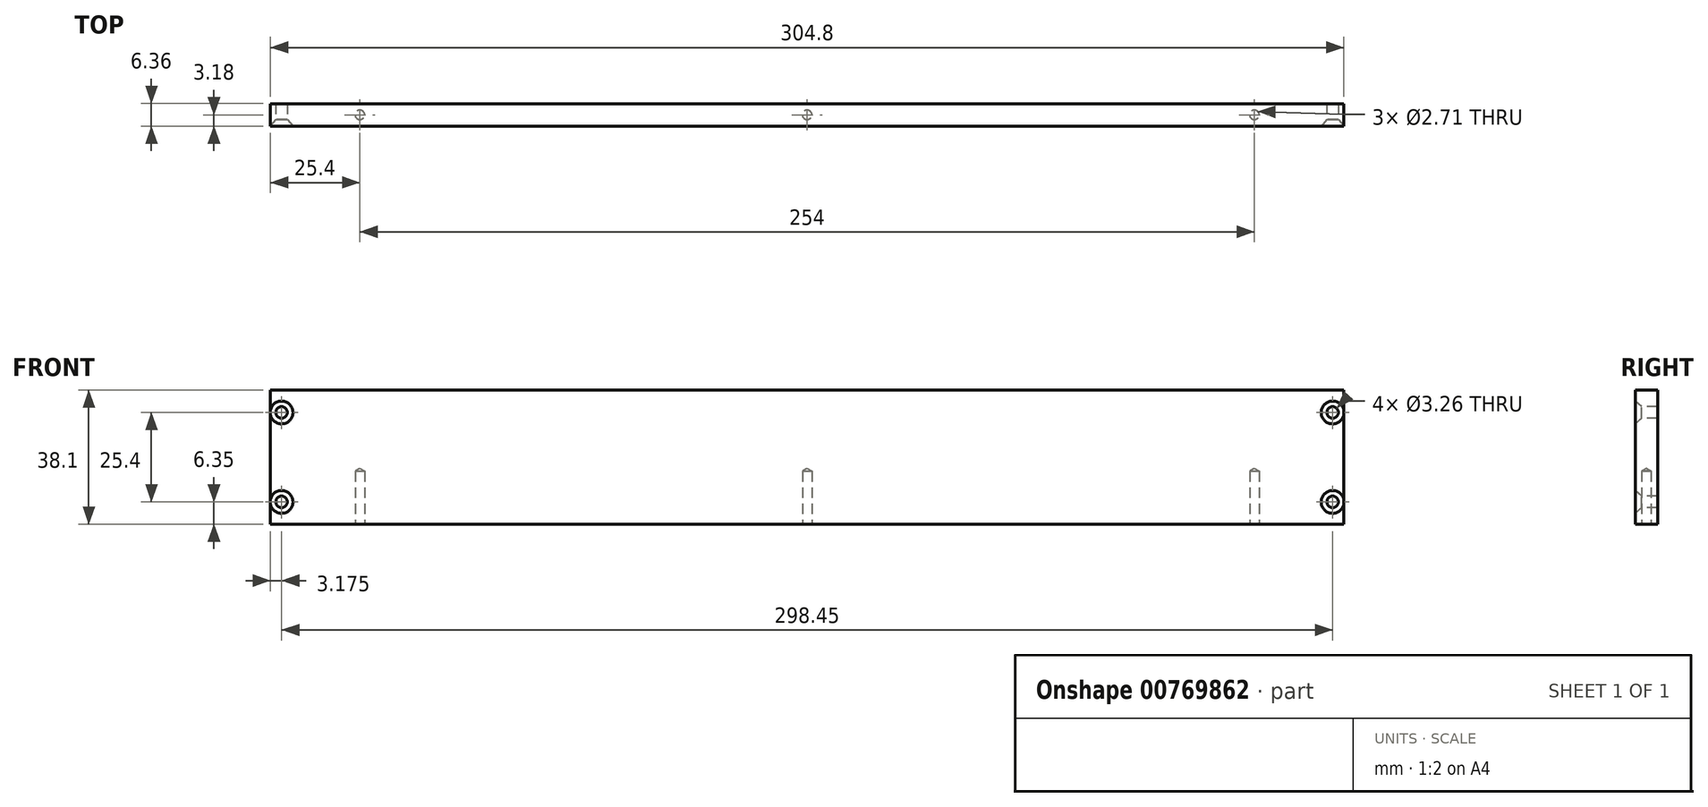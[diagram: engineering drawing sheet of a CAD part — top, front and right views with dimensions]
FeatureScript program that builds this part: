
annotation { "Feature Type Name" : "Feature", "Feature Type Description" : "" }
export const myFeature = defineFeature(function(context is Context, id is Id, definition is map)
    precondition{}
    {
        {
            var Q0;
            Q0=qCreatedBy(makeId("Top.planeOp"),FACE);
            var sketch = newSketch(context, id + "F0", { "sketchPlane" : qUnion([Q0])});
            skLineSegment(sketch, "E0.bottom", {"start": v(-152.4, 3.17) * mm, "end": v(152.4, 3.17) * mm});
            skLineSegment(sketch, "E0.top", {"start": v(-152.4, -3.18) * mm, "end": v(152.4, -3.18) * mm});
            skLineSegment(sketch, "E0.left", {"start": v(-152.4, 3.17) * mm, "end": v(-152.4, -3.18) * mm});
            skLineSegment(sketch, "E0.right", {"start": v(152.4, 3.17) * mm, "end": v(152.4, -3.18) * mm});
            skLineSegment(sketch, "E1", {"start": v(-152.4, 3.17) * mm, "end": v(152.4, -3.17) * mm, "construction": true});
            skSolve(sketch);
        }
        {
            var Q0;
            Q0=qSketchRegion(id+"F0",true);
            extrude(context, id + "F1", {"entities" : qUnion([Q0]), "depth" : 38.1 * mm, "offsetDistance" : 25.4 * mm});
        }
        {
            var Q0;
            Q0=makeQuery(id+"F1.opExtrude","CAP_FACE",FACE,{"disambiguationData":[OSD([sQuery(id+"F0.wireOp",EDGE,"E0.bottom"),sQuery(id+"F0.wireOp",EDGE,"E0.top"),sQuery(id+"F0.wireOp",EDGE,"E0.left"),sQuery(id+"F0.wireOp",EDGE,"E0.right")])],"isStart":true});
            var sketch = newSketch(context, id + "F2", { "sketchPlane" : qUnion([Q0])});
            skLineSegment(sketch, "E2", {"start": v(-152.4, 0) * mm, "end": v(152.4, 0) * mm, "construction": true});
            skPoint(sketch, "E3", {"position": v(-127, 0) * mm});
            skPoint(sketch, "E4", {"position": v(0, 0) * mm});
            skPoint(sketch, "E5", {"position": v(127, 0) * mm});
            skSolve(sketch);
        }
        {
            var Q0;
            Q0=sQuery(id+"F2.wireOp",VERTEX,"E3");
            var Q1;
            Q1=sQuery(id+"F2.wireOp",VERTEX,"E5");
            var Q2;
            Q2=sQuery(id+"F2.wireOp",VERTEX,"E4");
            var Q3;
            Q3=makeQuery(id+"F1.opExtrude","SWEPT_BODY",BODY,{"disambiguationData":[OSD([sQuery(id+"F0.wireOp",EDGE,"E0.bottom"),sQuery(id+"F0.wireOp",EDGE,"E0.top"),sQuery(id+"F0.wireOp",EDGE,"E0.left"),sQuery(id+"F0.wireOp",EDGE,"E0.right")])]});
            hole(context, id + "F3", {"style" : HoleStyle.SIMPLE, "endStyle" : HoleEndStyle.BLIND, "standardTappedOrClearance" : lookupTablePath({ "standard" : "ANSI", "engagement" : "75%", "pitch" : "32 tpi", "size" : "#6", "type" : "Tapped" }), "standardBlindInLast" : lookupTablePath({ "standard" : "ANSI", "engagement" : "75%", "pitch" : "32 tpi", "size" : "#6", "type" : "Tapped" }), "holeDiameter" : 2.7 * mm, "majorDiameter" : 3.5 * mm, "showTappedDepth" : true, "holeDepth" : 15.08 * mm, "tappedDepth" : 12.7 * mm, "tapClearance" : 3, "locations" : qUnion([Q0, Q1, Q2]), "scope" : qUnion([Q3])});
        }
        {
            var Q0;
            Q0=makeQuery(id+"F1.opExtrude","SWEPT_FACE",FACE,{"disambiguationData":[OSD([sQuery(id+"F0.wireOp",EDGE,"E0.top")])]});
            var sketch = newSketch(context, id + "F4", { "sketchPlane" : qUnion([Q0])});
            skLineSegment(sketch, "E6", {"start": v(-149.22, 38.1) * mm, "end": v(-149.22, 0) * mm, "construction": true});
            skLineSegment(sketch, "E7", {"start": v(149.22, 38.1) * mm, "end": v(149.22, 0) * mm, "construction": true});
            skPoint(sketch, "E8", {"position": v(-149.22, 31.75) * mm});
            skPoint(sketch, "E9", {"position": v(-149.22, 6.35) * mm});
            skPoint(sketch, "E10", {"position": v(149.22, 31.75) * mm});
            skPoint(sketch, "E11", {"position": v(149.22, 6.35) * mm});
            skPoint(sketch, "E12", {"position": v(-149.22, 19.05) * mm});
            skPoint(sketch, "E13", {"position": v(149.22, 19.05) * mm});
            skSolve(sketch);
        }
        {
            var Q0;
            Q0=sQuery(id+"F4.wireOp",VERTEX,"E8");
            var Q1;
            Q1=sQuery(id+"F4.wireOp",VERTEX,"E9");
            var Q2;
            Q2=sQuery(id+"F4.wireOp",VERTEX,"E10");
            var Q3;
            Q3=sQuery(id+"F4.wireOp",VERTEX,"E11");
            var Q4;
            Q4=makeQuery(id+"F1.opExtrude","SWEPT_BODY",BODY,{"disambiguationData":[OSD([sQuery(id+"F0.wireOp",EDGE,"E0.bottom"),sQuery(id+"F0.wireOp",EDGE,"E0.top"),sQuery(id+"F0.wireOp",EDGE,"E0.left"),sQuery(id+"F0.wireOp",EDGE,"E0.right")])]});
            hole(context, id + "F5", {"style" : HoleStyle.C_SINK, "endStyle" : HoleEndStyle.THROUGH, "standardTappedOrClearance" : lookupTablePath({ "standard" : "ANSI", "fit" : "Normal (ASME)", "size" : "#4", "type" : "Clearance" }), "standardBlindInLast" : lookupTablePath({ "fit" : "Free", "standard" : "ANSI", "size" : "#4", "type" : "Clearance" }), "holeDiameter" : 3.26 * mm, "cSinkDiameter" : 6.48 * mm, "cSinkAngle" : 82 * degree, "majorDiameter" : 2.84 * mm, "tappedDepth" : 11.84 * mm, "tapClearance" : 3, "startFromSketch" : true, "locations" : qUnion([Q0, Q1, Q2, Q3]), "scope" : qUnion([Q4])});
        }
    });
